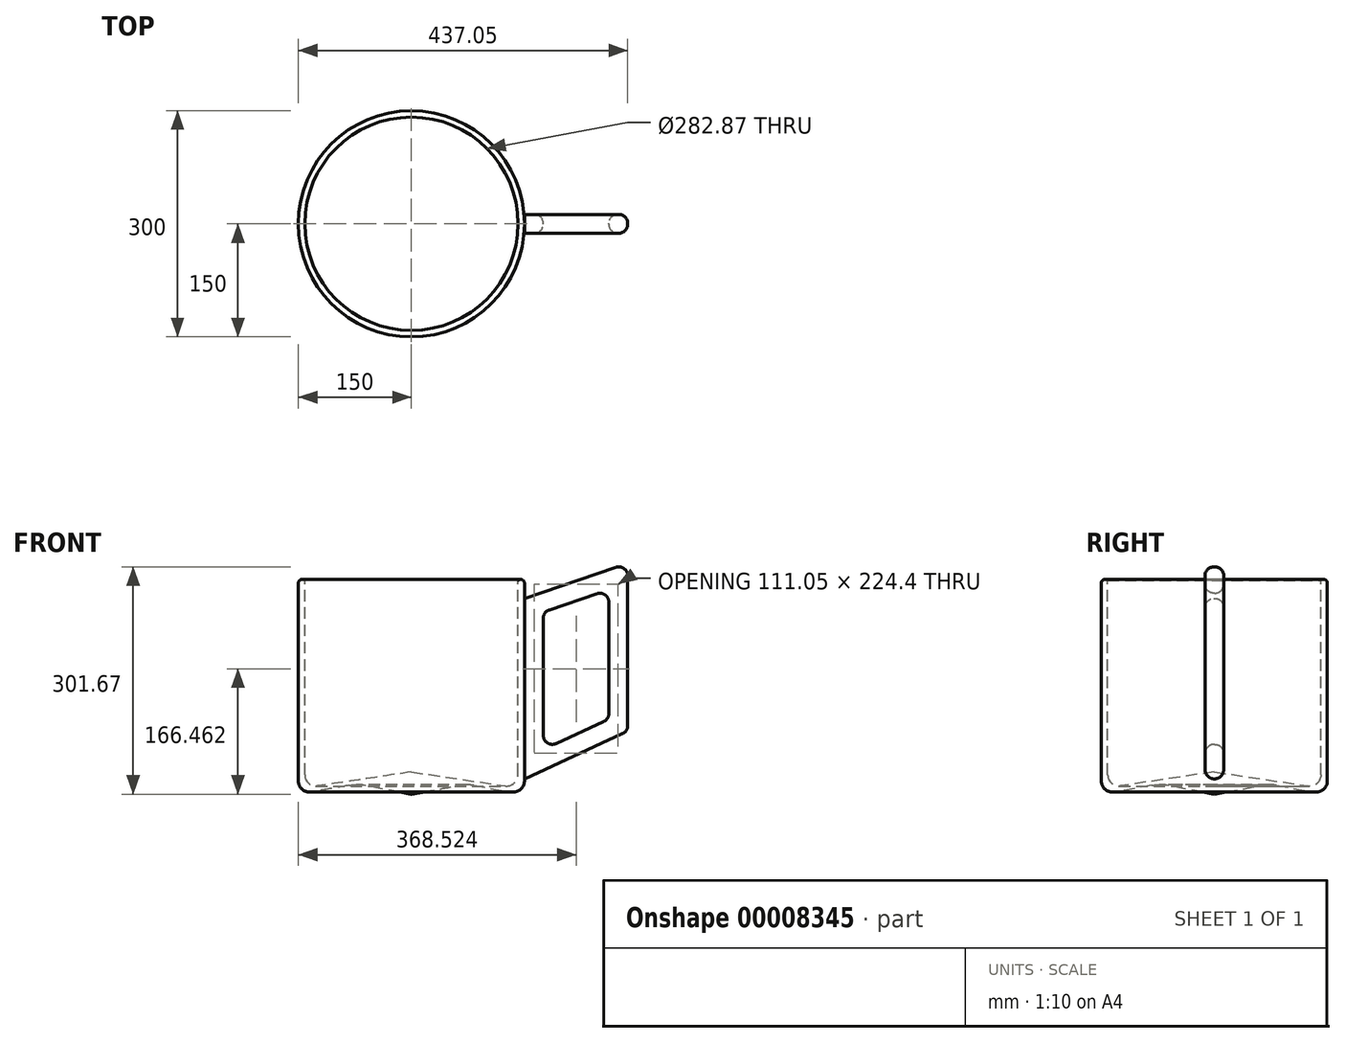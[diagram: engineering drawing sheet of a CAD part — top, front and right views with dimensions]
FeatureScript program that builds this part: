
annotation { "Feature Type Name" : "Feature", "Feature Type Description" : "" }
export const myFeature = defineFeature(function(context is Context, id is Id, definition is map)
    precondition{}
    {
        {
            var Q0;
            Q0=qCreatedBy(makeId("Front.planeOp"),FACE);
            var sketch = newSketch(context, id + "F0", { "sketchPlane" : qUnion([Q0])});
            skLineSegment(sketch, "E0", {"start": v(0, 0) * mm, "end": v(-72.92, 13.49) * mm});
            skLineSegment(sketch, "E1", {"start": v(-72.92, 13.49) * mm, "end": v(-150, 0) * mm});
            skLineSegment(sketch, "E2", {"start": v(-150, 0) * mm, "end": v(-150, 300) * mm});
            skLineSegment(sketch, "E3", {"start": v(-150, 300) * mm, "end": v(-141.43, 283.5) * mm});
            skLineSegment(sketch, "E4", {"start": v(-141.43, 283.5) * mm, "end": v(-141.43, 8.5) * mm});
            skLineSegment(sketch, "E5", {"start": v(-141.43, 8.5) * mm, "end": v(0, 29.72) * mm});
            skLineSegment(sketch, "E6", {"start": v(0, 29.72) * mm, "end": v(0, 0) * mm});
            skSolve(sketch);
        }
        {
            var Q0;
            Q0=makeQuery(id+"F0.imprint","IMPRINT",FACE,{"disambiguationData":[TD([[makeQuery(id+"F0.imprint","IMPRINT",EDGE,{"derivedFrom":sQuery(id+"F0.wireOp",EDGE,"E0")}),-1.0]])]});
            var Q1;
            Q1=sQuery(id+"F0.wireOp",EDGE,"E6");
            revolve(context, id + "F1", {"entities" : qUnion([Q0]), "axis" : qUnion([Q1]), "revolveType" : RevolveType.FULL});
        }
        {
            var Q0;
            Q0=qCreatedBy(makeId("Front.planeOp"),FACE);
            var sketch = newSketch(context, id + "F2", { "sketchPlane" : qUnion([Q0])});
            skLineSegment(sketch, "E7", {"start": v(150, 66.84) * mm, "end": v(150, 198.15) * mm});
            skLineSegment(sketch, "E8", {"start": v(150, 198.15) * mm, "end": v(150, 259.8) * mm});
            skLineSegment(sketch, "E9", {"start": v(150, 259.8) * mm, "end": v(287.05, 306.43) * mm});
            skLineSegment(sketch, "E10", {"start": v(287.05, 306.43) * mm, "end": v(287.05, 83.46) * mm});
            skLineSegment(sketch, "E11", {"start": v(150, 20.48) * mm, "end": v(287.05, 83.46) * mm});
            skLineSegment(sketch, "E12", {"start": v(150, 66.84) * mm, "end": v(150, 20.48) * mm});
            skLineSegment(sketch, "E13", {"start": v(175, 59.48) * mm, "end": v(175, 241.9) * mm});
            skLineSegment(sketch, "E14", {"start": v(175, 241.9) * mm, "end": v(262.05, 271.52) * mm});
            skLineSegment(sketch, "E15", {"start": v(262.05, 271.52) * mm, "end": v(262.05, 99.49) * mm});
            skLineSegment(sketch, "E16", {"start": v(262.05, 99.49) * mm, "end": v(175, 59.48) * mm});
            skSolve(sketch);
        }
        {
            var Q0;
            Q0 = qSketchRegion(id + "F2", true);
            extrude(context, id + "F3", {"entities" : qUnion([Q0]), "operationType" : NewBodyOperationType.ADD, "depth" : 12.5 * mm});
        }
        {
            var Q0;
            Q0=makeQuery(id+"F3.opExtrude","CAP_FACE",FACE,{"disambiguationData":[OSD([sQuery(id+"F2.wireOp",EDGE,"f54c332f-e132-4932-9c43-03510eb78c2d"),sQuery(id+"F2.wireOp",EDGE,"e70ff315-e076-487a-9730-234ae258735f"),sQuery(id+"F2.wireOp",EDGE,"E7"),sQuery(id+"F2.wireOp",EDGE,"8c6edb56-3c9a-4816-baf9-ee22acb7606c"),sQuery(id+"F2.wireOp",EDGE,"95e93eb1-de50-4a16-ad69-35b105c7e53e"),sQuery(id+"F2.wireOp",EDGE,"209c1aaf-e104-4006-ae7e-682cab1df452"),sQuery(id+"F2.wireOp",EDGE,"24d3c6a2-ac1c-4278-99c6-8ab21eb74ea6"),sQuery(id+"F2.wireOp",EDGE,"9568b977-8ee0-44b4-a06a-e79f10fc5cfb")])],"isStart":true});
            extrude(context, id + "F4", {"entities" : qUnion([Q0]), "operationType" : NewBodyOperationType.ADD, "depth" : 12.5 * mm});
        }
        {
            var Q0;
            Q0=makeQuery(id+"F1.opRevolve","SWEPT_EDGE",EDGE,{"disambiguationData":[OSD([sQuery(id+"F0.wireOp",EDGE,"E2"),sQuery(id+"F0.wireOp",EDGE,"E3")])]});
            fillet(context, id + "F5", {"entities" : qUnion([Q0]), "radius" : 5 * mm, "tangentPropagation" : true, "allowEdgeOverflow" : false});
        }
        {
            var Q0;
            Q0=makeQuery(id+"F1.opRevolve","SWEPT_EDGE",EDGE,{"disambiguationData":[OSD([sQuery(id+"F0.wireOp",EDGE,"E4"),sQuery(id+"F0.wireOp",EDGE,"E5")])]});
            fillet(context, id + "F6", {"entities" : qUnion([Q0]), "radius" : 15 * mm, "tangentPropagation" : true, "allowEdgeOverflow" : false});
        }
        {
            var Q0;
            Q0=makeQuery(id+"F1.opRevolve","SWEPT_EDGE",EDGE,{"disambiguationData":[OSD([sQuery(id+"F0.wireOp",EDGE,"E1"),sQuery(id+"F0.wireOp",EDGE,"E2")])]});
            fillet(context, id + "F7", {"entities" : qUnion([Q0]), "radius" : 15 * mm, "tangentPropagation" : true, "allowEdgeOverflow" : false});
        }
        {
            var Q0;
            Q0=makeQuery(id+"F1.opRevolve","SWEPT_EDGE",EDGE,{"disambiguationData":[OSD([sQuery(id+"F0.wireOp",EDGE,"E0"),sQuery(id+"F0.wireOp",EDGE,"E1")])]});
            fillet(context, id + "F8", {"entities" : qUnion([Q0]), "radius" : 55 * mm, "tangentPropagation" : true, "allowEdgeOverflow" : false});
        }
        {
            var Q0;
            Q0=makeQuery(id+"F3.opExtrude","CAP_EDGE",EDGE,{"disambiguationData":[OSD([sQuery(id+"F2.wireOp",EDGE,"E13")])],"isStart":false});
            var Q1;
            Q1=makeQuery(id+"F4.opExtrude","CAP_EDGE",EDGE,{"disambiguationData":[OSD([sQuery(id+"F2.wireOp",EDGE,"E13")])],"isStart":false});
            var Q2;
            Q2=makeQuery(id+"F3.opExtrude","CAP_EDGE",EDGE,{"disambiguationData":[OSD([sQuery(id+"F2.wireOp",EDGE,"E14")])],"isStart":false});
            var Q3;
            Q3=makeQuery(id+"F4.opExtrude","CAP_EDGE",EDGE,{"disambiguationData":[OSD([sQuery(id+"F2.wireOp",EDGE,"E14")])],"isStart":false});
            var Q4;
            Q4=makeQuery(id+"F4.opExtrude","CAP_EDGE",EDGE,{"disambiguationData":[OSD([sQuery(id+"F2.wireOp",EDGE,"E15")])],"isStart":false});
            var Q5;
            Q5=makeQuery(id+"F3.opExtrude","CAP_EDGE",EDGE,{"disambiguationData":[OSD([sQuery(id+"F2.wireOp",EDGE,"E15")])],"isStart":false});
            var Q6;
            Q6=makeQuery(id+"F4.opExtrude","CAP_EDGE",EDGE,{"disambiguationData":[OSD([sQuery(id+"F2.wireOp",EDGE,"E16")])],"isStart":false});
            var Q7;
            Q7=makeQuery(id+"F3.opExtrude","CAP_EDGE",EDGE,{"disambiguationData":[OSD([sQuery(id+"F2.wireOp",EDGE,"E16")])],"isStart":false});
            var Q8;
            Q8=makeQuery(id+"F3.opExtrude","CAP_EDGE",EDGE,{"disambiguationData":[OSD([sQuery(id+"F2.wireOp",EDGE,"E11")])],"isStart":false});
            var Q9;
            Q9=makeQuery(id+"F4.opExtrude","CAP_EDGE",EDGE,{"disambiguationData":[OSD([sQuery(id+"F2.wireOp",EDGE,"E11")])],"isStart":false});
            var Q10;
            Q10=makeQuery(id+"F4.opExtrude","CAP_EDGE",EDGE,{"disambiguationData":[OSD([sQuery(id+"F2.wireOp",EDGE,"E10")])],"isStart":false});
            var Q11;
            Q11=makeQuery(id+"F3.opExtrude","CAP_EDGE",EDGE,{"disambiguationData":[OSD([sQuery(id+"F2.wireOp",EDGE,"E10")])],"isStart":false});
            var Q12;
            Q12=makeQuery(id+"F4.opExtrude","CAP_EDGE",EDGE,{"disambiguationData":[OSD([sQuery(id+"F2.wireOp",EDGE,"E9")])],"isStart":false});
            var Q13;
            Q13=makeQuery(id+"F3.opExtrude","CAP_EDGE",EDGE,{"disambiguationData":[OSD([sQuery(id+"F2.wireOp",EDGE,"E9")])],"isStart":false});
            var Q14;
            Q14=makeQuery(id+"F3.opExtrude","SWEPT_EDGE",EDGE,{"disambiguationData":[OSD([sQuery(id+"F2.wireOp",EDGE,"E9"),sQuery(id+"F2.wireOp",EDGE,"E10")])]});
            var Q15;
            Q15=makeQuery(id+"F4.opExtrude","SWEPT_EDGE",EDGE,{"disambiguationData":[OSD([sQuery(id+"F2.wireOp",EDGE,"E9"),sQuery(id+"F2.wireOp",EDGE,"E10")])]});
            var Q16;
            Q16=makeQuery(id+"F4.opExtrude","SWEPT_EDGE",EDGE,{"disambiguationData":[OSD([sQuery(id+"F2.wireOp",EDGE,"E10"),sQuery(id+"F2.wireOp",EDGE,"E11")])]});
            var Q17;
            Q17=makeQuery(id+"F3.opExtrude","SWEPT_EDGE",EDGE,{"disambiguationData":[OSD([sQuery(id+"F2.wireOp",EDGE,"E10"),sQuery(id+"F2.wireOp",EDGE,"E11")])]});
            var Q18;
            Q18=makeQuery(id+"F4.opExtrude","SWEPT_EDGE",EDGE,{"disambiguationData":[OSD([sQuery(id+"F2.wireOp",EDGE,"E15"),sQuery(id+"F2.wireOp",EDGE,"E16")])]});
            var Q19;
            Q19=makeQuery(id+"F3.opExtrude","SWEPT_EDGE",EDGE,{"disambiguationData":[OSD([sQuery(id+"F2.wireOp",EDGE,"E15"),sQuery(id+"F2.wireOp",EDGE,"E16")])]});
            var Q20;
            Q20=makeQuery(id+"F4.opExtrude","SWEPT_EDGE",EDGE,{"disambiguationData":[OSD([sQuery(id+"F2.wireOp",EDGE,"E14"),sQuery(id+"F2.wireOp",EDGE,"E15")])]});
            var Q21;
            Q21=makeQuery(id+"F3.opExtrude","SWEPT_EDGE",EDGE,{"disambiguationData":[OSD([sQuery(id+"F2.wireOp",EDGE,"E14"),sQuery(id+"F2.wireOp",EDGE,"E15")])]});
            var Q22;
            Q22=makeQuery(id+"F4.opExtrude","SWEPT_EDGE",EDGE,{"disambiguationData":[OSD([sQuery(id+"F2.wireOp",EDGE,"E13"),sQuery(id+"F2.wireOp",EDGE,"E14")])]});
            var Q23;
            Q23=makeQuery(id+"F3.opExtrude","SWEPT_EDGE",EDGE,{"disambiguationData":[OSD([sQuery(id+"F2.wireOp",EDGE,"E13"),sQuery(id+"F2.wireOp",EDGE,"E14")])]});
            var Q24;
            Q24=makeQuery(id+"F4.opExtrude","SWEPT_EDGE",EDGE,{"disambiguationData":[OSD([sQuery(id+"F2.wireOp",EDGE,"E13"),sQuery(id+"F2.wireOp",EDGE,"E16")])]});
            var Q25;
            Q25=makeQuery(id+"F3.opExtrude","SWEPT_EDGE",EDGE,{"disambiguationData":[OSD([sQuery(id+"F2.wireOp",EDGE,"E13"),sQuery(id+"F2.wireOp",EDGE,"E16")])]});
            fillet(context, id + "F9", {"entities" : qUnion([Q0, Q1, Q2, Q3, Q4, Q5, Q6, Q7, Q8, Q9, Q10, Q11, Q12, Q13, Q14, Q15, Q16, Q17, Q18, Q19, Q20, Q21, Q22, Q23, Q24, Q25]), "radius" : 12 * mm, "tangentPropagation" : true, "allowEdgeOverflow" : false});
        }
    });
